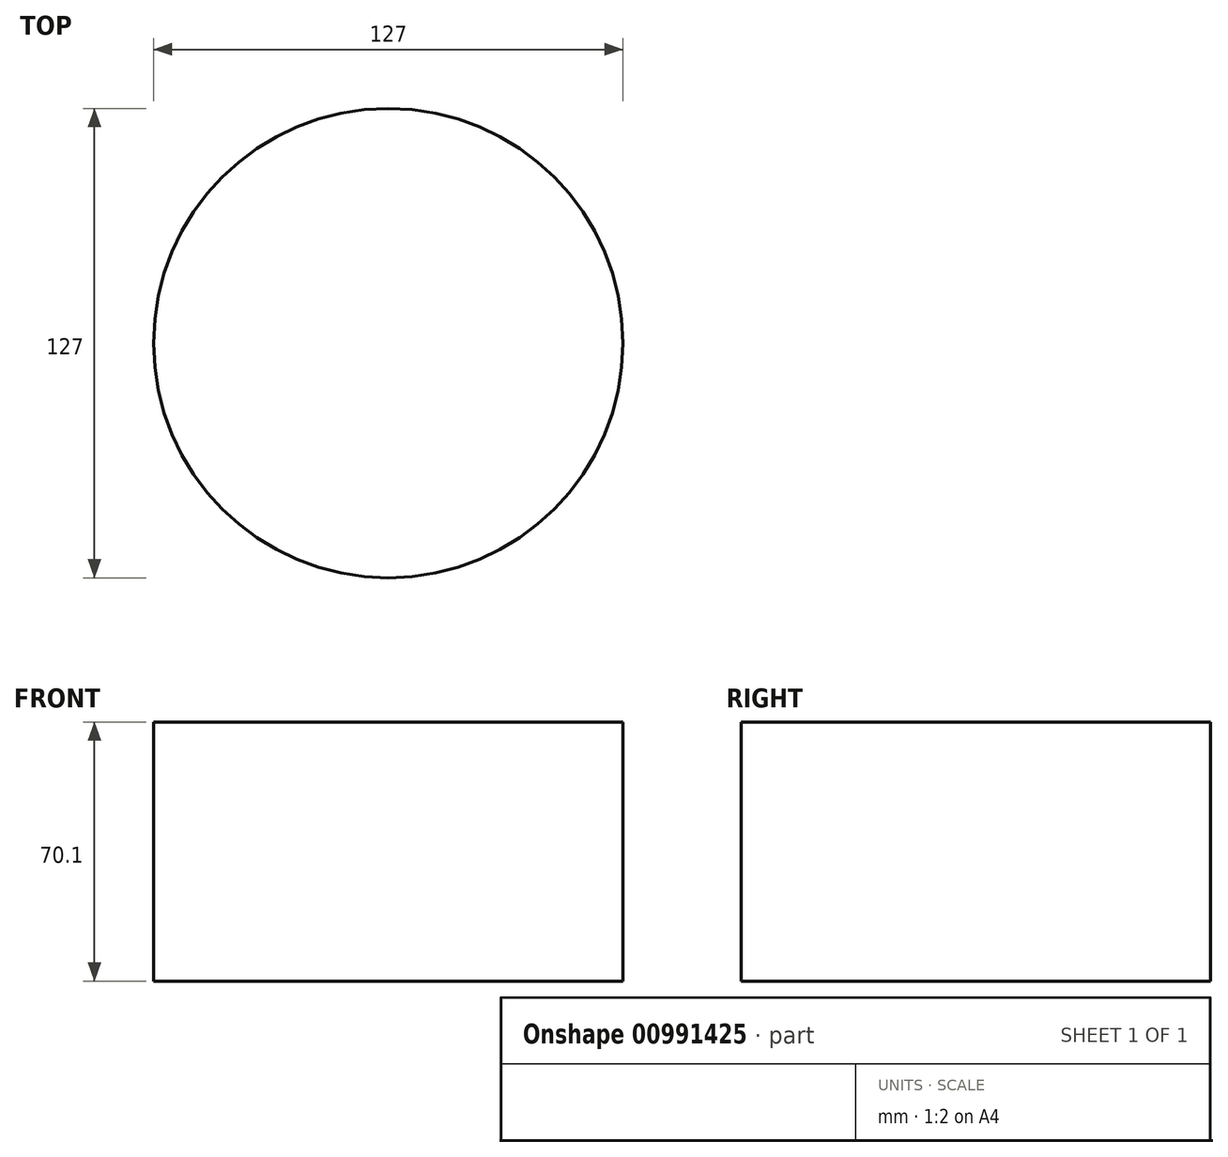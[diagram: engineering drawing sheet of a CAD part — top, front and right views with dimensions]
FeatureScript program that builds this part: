
annotation { "Feature Type Name" : "Feature", "Feature Type Description" : "" }
export const myFeature = defineFeature(function(context is Context, id is Id, definition is map)
    precondition{}
    {
        {
            var Q0;
            Q0=qCreatedBy(makeId("Top.planeOp"),FACE);
            var sketch = newSketch(context, id + "F0", { "sketchPlane" : qUnion([Q0])});
            skCircle(sketch, "E0", {"center": v(0, 0) * mm, "radius": 63.5 * mm});
            skSolve(sketch);
        }
        {
            var Q0;
            Q0 = qSketchRegion(id + "F0", true);
            extrude(context, id + "F1", {"entities" : qUnion([Q0]), "oppositeDirection" : true, "depth" : 70.1 * mm, "offsetDistance" : 25.4 * mm});
        }
        {
            var Q0;
            Q0=qCreatedBy(makeId("Right.planeOp"),FACE);
            cPlane(context, id + "F2", {"entities" : qUnion([Q0]), "cplaneType" : CPlaneType.OFFSET, "offset" : 94.23 * mm, "width" : 152.4 * mm, "height" : 152.4 * mm});
        }
    });
